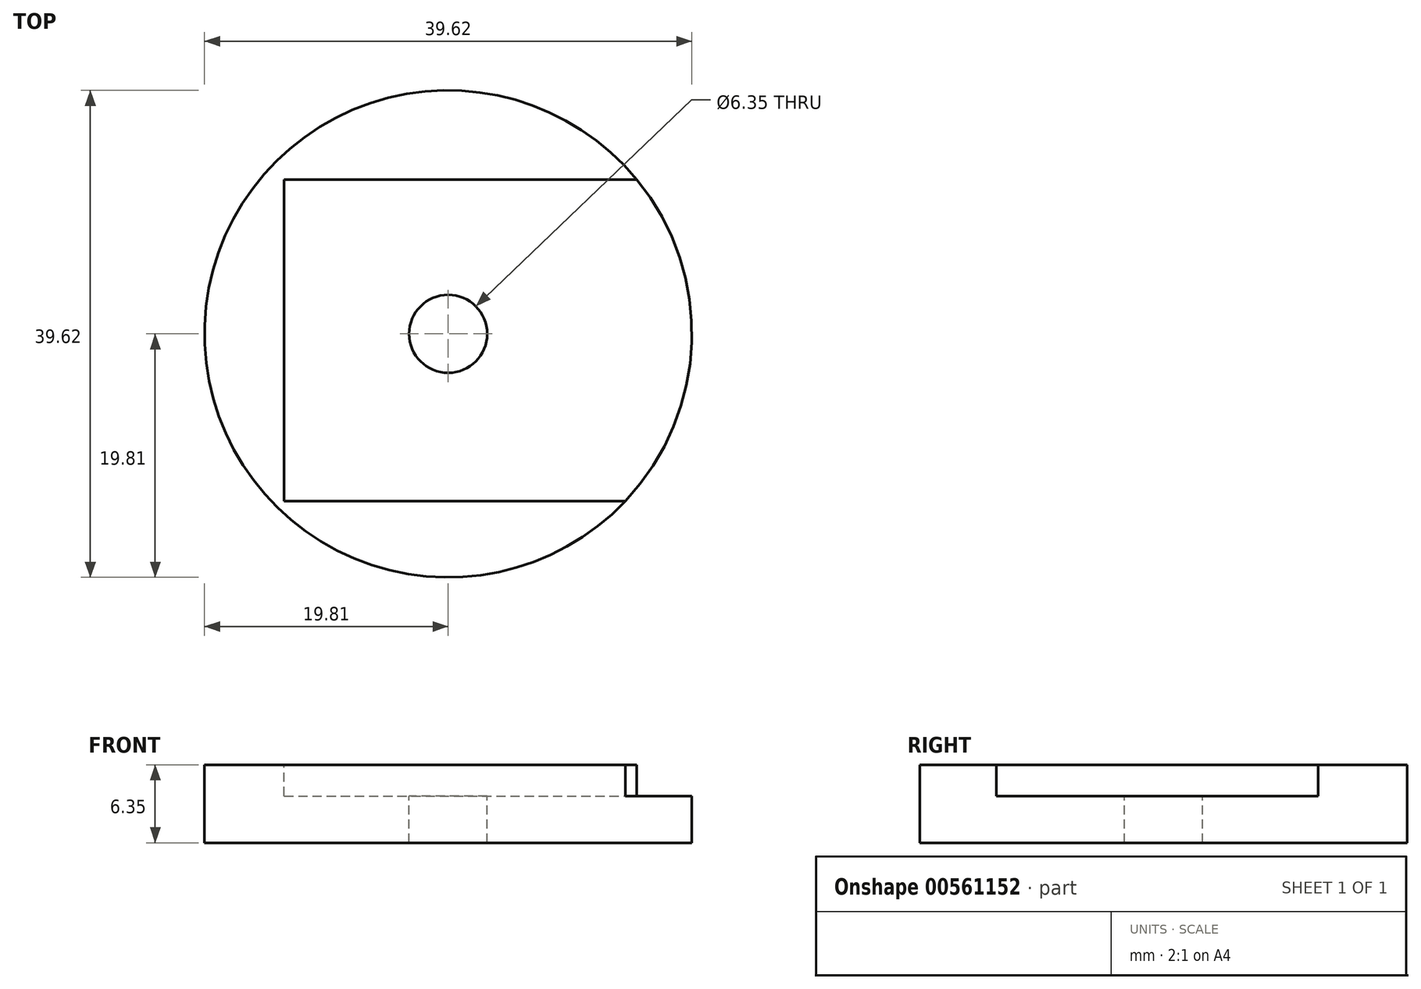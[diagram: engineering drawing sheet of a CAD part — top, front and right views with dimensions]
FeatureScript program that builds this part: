
annotation { "Feature Type Name" : "Feature", "Feature Type Description" : "" }
export const myFeature = defineFeature(function(context is Context, id is Id, definition is map)
    precondition{}
    {
        {
            var Q0;
            Q0=qCreatedBy(makeId("Top.planeOp"),FACE);
            var sketch = newSketch(context, id + "F0", { "sketchPlane" : qUnion([Q0])});
            skCircle(sketch, "E0", {"center": v(0, 0) * mm, "radius": 19.81 * mm});
            skSolve(sketch);
        }
        {
            var Q0;
            Q0=makeQuery(id+"F0.imprint","IMPRINT",FACE,{"disambiguationData":[TD([[makeQuery(id+"F0.imprint","IMPRINT",EDGE,{"derivedFrom":sQuery(id+"F0.wireOp",EDGE,"E0")}),1.0]])]});
            extrude(context, id + "F1", {"entities" : qUnion([Q0]), "depth" : 6.35 * mm, "offsetDistance" : 25.4 * mm});
        }
        {
            var Q0;
            Q0=makeQuery(id+"F1.opExtrude","CAP_FACE",FACE,{"disambiguationData":[OSD([sQuery(id+"F0.wireOp",EDGE,"E0")])],"isStart":false});
            var sketch = newSketch(context, id + "F2", { "sketchPlane" : qUnion([Q0])});
            skCircle(sketch, "E1", {"center": v(0, 0) * mm, "radius": 3.18 * mm});
            skSolve(sketch);
        }
        {
            var Q0;
            Q0 = qSketchRegion(id + "F2", true);
            extrude(context, id + "F3", {"entities" : qUnion([Q0]), "operationType" : NewBodyOperationType.REMOVE, "oppositeDirection" : true, "depth" : 25.4 * mm, "offsetDistance" : 25.4 * mm});
        }
        {
            var Q0;
            Q0=makeQuery(id+"F1.opExtrude","CAP_FACE",FACE,{"disambiguationData":[OSD([sQuery(id+"F0.wireOp",EDGE,"E0")])],"isStart":false});
            var sketch = newSketch(context, id + "F4", { "sketchPlane" : qUnion([Q0])});
            skLineSegment(sketch, "E2.bottom", {"start": v(-13.34, 12.56) * mm, "end": v(20.96, 12.56) * mm});
            skLineSegment(sketch, "E2.top", {"start": v(-13.34, -13.6) * mm, "end": v(20.96, -13.6) * mm});
            skLineSegment(sketch, "E2.left", {"start": v(-13.34, 12.56) * mm, "end": v(-13.34, -13.6) * mm});
            skLineSegment(sketch, "E2.right", {"start": v(20.96, 12.56) * mm, "end": v(20.96, -13.6) * mm});
            skSolve(sketch);
        }
        {
            var Q0;
            Q0 = qSketchRegion(id + "F4", true);
            extrude(context, id + "F5", {"entities" : qUnion([Q0]), "operationType" : NewBodyOperationType.REMOVE, "oppositeDirection" : true, "depth" : 2.54 * mm, "offsetDistance" : 25.4 * mm});
        }
    });
